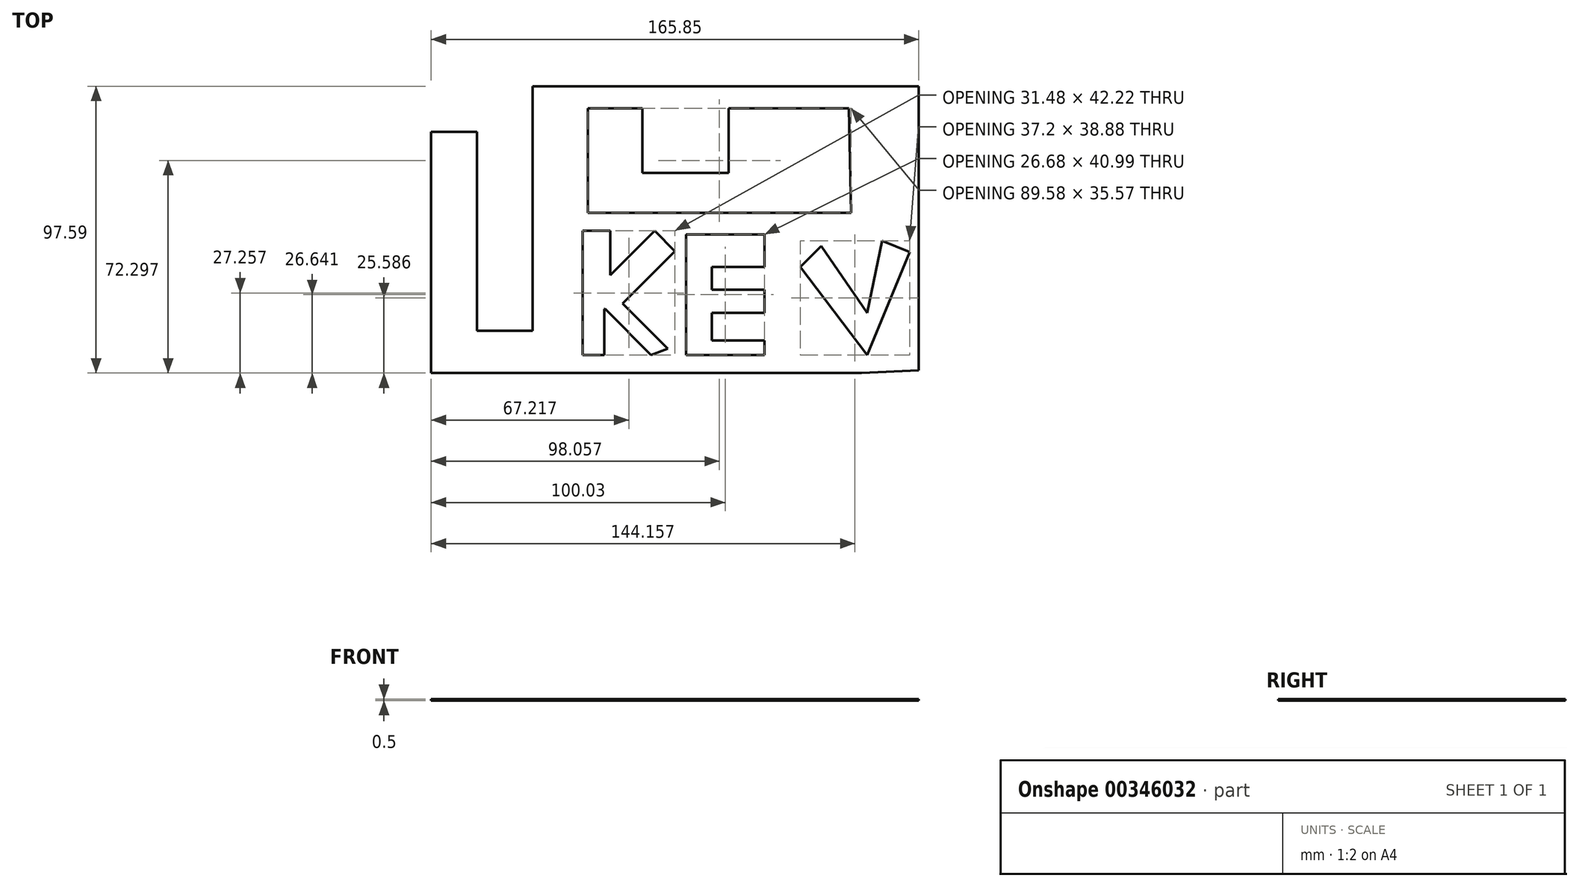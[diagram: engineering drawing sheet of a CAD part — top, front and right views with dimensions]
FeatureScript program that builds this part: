
annotation { "Feature Type Name" : "Feature", "Feature Type Description" : "" }
export const myFeature = defineFeature(function(context is Context, id is Id, definition is map)
    precondition{}
    {
        {
            var Q0;
            Q0=qCreatedBy(makeId("Top.planeOp"),FACE);
            var sketch = newSketch(context, id + "F0", { "sketchPlane" : qUnion([Q0])});
            skPoint(sketch, "E0.start.orphan", {"position": v(-84.43, -44.96) * mm});
            skLineSegment(sketch, "E1", {"start": v(-71.82, 38.89) * mm, "end": v(-71.82, -43.18) * mm});
            skLineSegment(sketch, "E2", {"start": v(-71.82, -43.18) * mm, "end": v(-49.4, -43.18) * mm});
            skLineSegment(sketch, "E3", {"start": v(74.58, -43.18) * mm, "end": v(-49.4, -43.18) * mm});
            skLineSegment(sketch, "E4", {"start": v(-71.82, 38.89) * mm, "end": v(-66.87, 38.89) * mm});
            skLineSegment(sketch, "E5", {"start": v(-66.87, 38.89) * mm, "end": v(-56.24, 38.89) * mm});
            skLineSegment(sketch, "E6", {"start": v(-56.24, 38.89) * mm, "end": v(-56.24, -28.8) * mm});
            skLineSegment(sketch, "E7", {"start": v(-56.24, -28.8) * mm, "end": v(-37.34, -28.8) * mm});
            skLineSegment(sketch, "E8", {"start": v(-37.34, -28.8) * mm, "end": v(-37.34, 54.4) * mm});
            skLineSegment(sketch, "E9", {"start": v(-37.34, 54.4) * mm, "end": v(94.03, 54.4) * mm});
            skLineSegment(sketch, "E10", {"start": v(94.03, 54.4) * mm, "end": v(94.03, -42.21) * mm});
            skLineSegment(sketch, "E11", {"start": v(74.58, -43.18) * mm, "end": v(94.03, -42.21) * mm});
            skLineSegment(sketch, "E12", {"start": v(-18.55, 46.9) * mm, "end": v(-18.55, 11.33) * mm});
            skLineSegment(sketch, "E13", {"start": v(-18.55, 11.33) * mm, "end": v(71.03, 11.33) * mm});
            skLineSegment(sketch, "E14", {"start": v(-18.55, 46.9) * mm, "end": v(0, 46.9) * mm});
            skLineSegment(sketch, "E15", {"start": v(0, 46.9) * mm, "end": v(0, 24.9) * mm});
            skLineSegment(sketch, "E16", {"start": v(0, 24.9) * mm, "end": v(29.3, 24.9) * mm});
            skLineSegment(sketch, "E17", {"start": v(29.3, 24.9) * mm, "end": v(29.3, 46.9) * mm});
            skLineSegment(sketch, "E18", {"start": v(29.3, 46.9) * mm, "end": v(70.26, 46.9) * mm});
            skLineSegment(sketch, "E19", {"start": v(70.26, 46.9) * mm, "end": v(71.03, 11.33) * mm});
            skLineSegment(sketch, "E20", {"start": v(-20.34, 5.19) * mm, "end": v(-20.34, -34.48) * mm});
            skLineSegment(sketch, "E21", {"start": v(-20.34, 5.19) * mm, "end": v(-10.87, 5.19) * mm});
            skLineSegment(sketch, "E22", {"start": v(-10.87, 5.19) * mm, "end": v(-10.87, -9.91) * mm});
            skLineSegment(sketch, "E23", {"start": v(-10.87, -9.91) * mm, "end": v(4.23, 5.19) * mm});
            skLineSegment(sketch, "E24", {"start": v(4.23, 5.19) * mm, "end": v(11.14, -1.72) * mm});
            skLineSegment(sketch, "E25", {"start": v(11.14, -1.72) * mm, "end": v(-6.65, -19.51) * mm});
            skLineSegment(sketch, "E26", {"start": v(-6.65, -19.51) * mm, "end": v(8.7, -34.87) * mm});
            skLineSegment(sketch, "E27", {"start": v(8.7, -34.87) * mm, "end": v(2.97, -37.03) * mm});
            skLineSegment(sketch, "E28", {"start": v(2.97, -37.03) * mm, "end": v(-12.73, -21.34) * mm});
            skLineSegment(sketch, "E29", {"start": v(-12.88, -21.49) * mm, "end": v(-12.88, -37.03) * mm});
            skLineSegment(sketch, "E30", {"start": v(-20.34, -34.48) * mm, "end": v(-20.34, -37.03) * mm});
            skLineSegment(sketch, "E31", {"start": v(-20.34, -37.03) * mm, "end": v(-12.88, -37.03) * mm});
            skLineSegment(sketch, "E32", {"start": v(14.87, 3.95) * mm, "end": v(14.87, -37.03) * mm});
            skLineSegment(sketch, "E33", {"start": v(14.87, 3.95) * mm, "end": v(41.55, 3.95) * mm});
            skLineSegment(sketch, "E34", {"start": v(41.55, 3.95) * mm, "end": v(41.55, -7.12) * mm});
            skLineSegment(sketch, "E35", {"start": v(41.55, -7.12) * mm, "end": v(23.67, -7.12) * mm});
            skLineSegment(sketch, "E36", {"start": v(23.67, -7.12) * mm, "end": v(23.67, -14.78) * mm});
            skLineSegment(sketch, "E37", {"start": v(23.67, -14.78) * mm, "end": v(41.55, -14.78) * mm});
            skLineSegment(sketch, "E38", {"start": v(41.55, -14.78) * mm, "end": v(41.55, -22.73) * mm});
            skLineSegment(sketch, "E39", {"start": v(41.55, -22.73) * mm, "end": v(23.67, -22.73) * mm});
            skLineSegment(sketch, "E40", {"start": v(23.67, -22.73) * mm, "end": v(23.67, -32.1) * mm});
            skLineSegment(sketch, "E41", {"start": v(23.67, -32.1) * mm, "end": v(41.55, -32.1) * mm});
            skLineSegment(sketch, "E42", {"start": v(41.55, -32.1) * mm, "end": v(41.55, -37.03) * mm});
            skLineSegment(sketch, "E43", {"start": v(14.87, -37.03) * mm, "end": v(41.55, -37.03) * mm});
            skLineSegment(sketch, "E44", {"start": v(60.85, 0) * mm, "end": v(53.74, -7.12) * mm});
            skLineSegment(sketch, "E45", {"start": v(53.74, -7.12) * mm, "end": v(76.46, -37.03) * mm});
            skLineSegment(sketch, "E46", {"start": v(76.46, -37.03) * mm, "end": v(90.94, -2) * mm});
            skLineSegment(sketch, "E47", {"start": v(90.94, -2) * mm, "end": v(81.62, 1.85) * mm});
            skLineSegment(sketch, "E48", {"start": v(81.62, 1.85) * mm, "end": v(76.46, -22.73) * mm});
            skLineSegment(sketch, "E49", {"start": v(76.46, -22.73) * mm, "end": v(60.85, 0) * mm});
            skLineSegment(sketch, "E50", {"start": v(-12.88, -21.49) * mm, "end": v(-12.73, -21.34) * mm});
            skSolve(sketch);
        }
        {
            var Q0;
            Q0=makeQuery(id+"F0.imprint","IMPRINT",FACE,{"disambiguationData":[TD([[makeQuery(id+"F0.imprint","IMPRINT",EDGE,{"derivedFrom":sQuery(id+"F0.wireOp",EDGE,"E1")}),1.0]])]});
            extrude(context, id + "F1", {"entities" : qUnion([Q0]), "depth" : 0.5 * mm});
        }
    });
